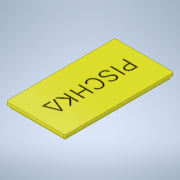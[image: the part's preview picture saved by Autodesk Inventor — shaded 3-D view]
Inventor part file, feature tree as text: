
AUTODESK INVENTOR PART (.ipt)
format: ipt  version: 2020.1 (Build 241239000, 239)  size: 467,968 bytes
history: native  units: mm
features: sketch x3, extrude x2, other x1, emboss x1
ambient origin geometry x8: Origin, YZ Plane, XZ Plane, XY Plane, X Axis, Y Axis, Z Axis, Center Point
bodies: Body1 (feature_tree)
feature tree (7):
  other  "Receiver Case.ipt"
  sketch  "Sketch3"  dims[d9=2.0mm d10=0.0mm d11=2.0mm d12=0.0mm]
  extrude  "Extrusion3"  Depth=0.4mm
  extrude  "Extrusion4"  Depth=2.0mm TaperAngle=0.0deg
  emboss  "Emboss1"
  sketch  "Sketch1_1"  dims[d0=10.0mm d8=0.4mm]
  sketch  "Sketch4"  dims[d13=0.4mm d14=0.0mm d15=0.15mm d16=0.15mm d17=0.15mm d18=0.15mm d19=0.8mm]
